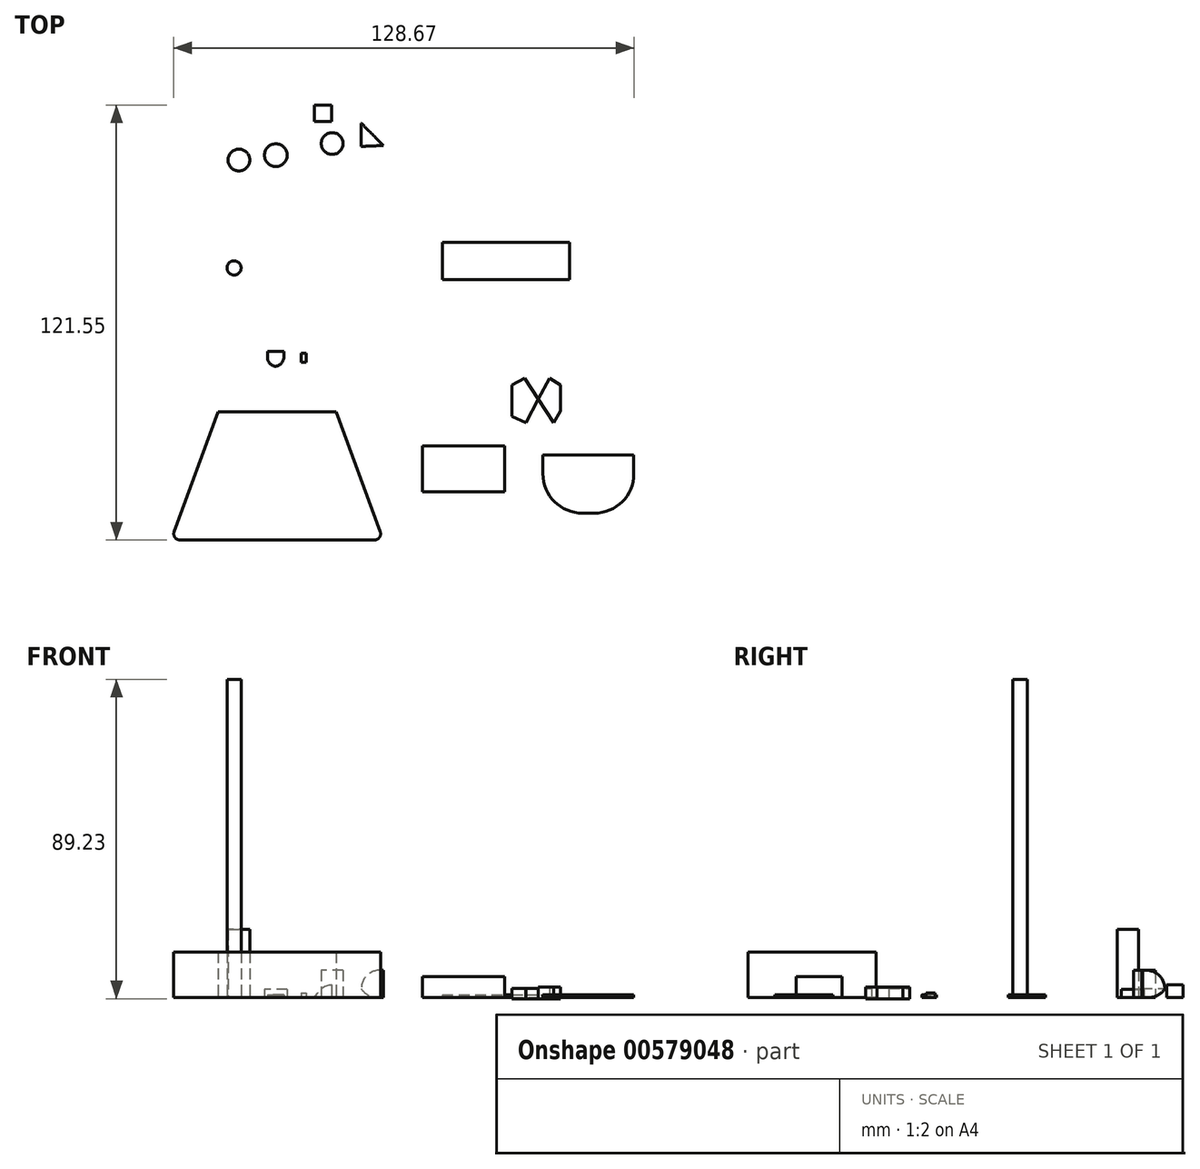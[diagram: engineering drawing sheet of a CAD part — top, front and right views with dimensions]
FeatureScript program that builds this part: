
annotation { "Feature Type Name" : "Feature", "Feature Type Description" : "" }
export const myFeature = defineFeature(function(context is Context, id is Id, definition is map)
    precondition{}
    {
        {
            var Q0;
            Q0=qCreatedBy(makeId("Top.planeOp"),FACE);
            var sketch = newSketch(context, id + "F0", { "sketchPlane" : qUnion([Q0])});
            skLineSegment(sketch, "E0", {"start": v(-46.16, -23.7) * mm, "end": v(-59.3, -59.45) * mm});
            skLineSegment(sketch, "E1", {"start": v(-59.3, -59.45) * mm, "end": v(0, -59.45) * mm});
            skLineSegment(sketch, "E2", {"start": v(0, -59.45) * mm, "end": v(-13.14, -23.7) * mm});
            skLineSegment(sketch, "E3", {"start": v(-13.14, -23.7) * mm, "end": v(-46.16, -23.7) * mm});
            skSolve(sketch);
        }
        {
            var Q0;
            Q0=makeQuery(id+"F0.imprint","IMPRINT",FACE,{"disambiguationData":[TD([[makeQuery(id+"F0.imprint","IMPRINT",EDGE,{"derivedFrom":sQuery(id+"F0.wireOp",EDGE,"E0")}),1.0]])]});
            extrude(context, id + "F1", {"entities" : qUnion([Q0]), "depth" : 12.7 * mm, "offsetDistance" : 25.4 * mm});
        }
        {
            var Q0;
            Q0=makeQuery(id+"F1.opExtrude","SWEPT_EDGE",EDGE,{"disambiguationData":[OSD([sQuery(id+"F0.wireOp",EDGE,"E0"),sQuery(id+"F0.wireOp",EDGE,"E1")])]});
            fillet(context, id + "F2", {"entities" : qUnion([Q0]), "radius" : 1.7 * mm, "tangentPropagation" : true, "allowEdgeOverflow" : false});
        }
        {
            var Q0;
            Q0=makeQuery(id+"F1.opExtrude","SWEPT_EDGE",EDGE,{"disambiguationData":[OSD([sQuery(id+"F0.wireOp",EDGE,"E1"),sQuery(id+"F0.wireOp",EDGE,"E2")])]});
            fillet(context, id + "F3", {"entities" : qUnion([Q0]), "radius" : 1.7 * mm, "tangentPropagation" : true, "allowEdgeOverflow" : false});
        }
        {
            var Q0;
            Q0=qCreatedBy(makeId("Top.planeOp"),FACE);
            var sketch = newSketch(context, id + "F4", { "sketchPlane" : qUnion([Q0])});
            skLineSegment(sketch, "E4.bottom", {"start": v(11.02, -33.17) * mm, "end": v(33.98, -33.17) * mm});
            skLineSegment(sketch, "E4.top", {"start": v(11.02, -46.03) * mm, "end": v(33.98, -46.03) * mm});
            skLineSegment(sketch, "E4.left", {"start": v(11.02, -33.17) * mm, "end": v(11.02, -46.03) * mm});
            skLineSegment(sketch, "E4.right", {"start": v(33.98, -33.17) * mm, "end": v(33.98, -46.03) * mm});
            skSolve(sketch);
        }
        {
            var Q0;
            Q0=makeQuery(id+"F4.imprint","IMPRINT",FACE,{"disambiguationData":[TD([[makeQuery(id+"F4.imprint","IMPRINT",EDGE,{"derivedFrom":sQuery(id+"F4.wireOp",EDGE,"E4.bottom")}),-1.0]])]});
            extrude(context, id + "F5", {"entities" : qUnion([Q0]), "depth" : 0.76 * mm, "offsetDistance" : 25.4 * mm});
        }
        {
            var Q0;
            Q0=qCreatedBy(makeId("Top.planeOp"),FACE);
            var sketch = newSketch(context, id + "F6", { "sketchPlane" : qUnion([Q0])});
            skLineSegment(sketch, "E5.bottom", {"start": v(-27.78, -6.77) * mm, "end": v(-32.37, -6.77) * mm});
            skLineSegment(sketch, "E5.top", {"start": v(-27.78, -10.9) * mm, "end": v(-32.37, -10.9) * mm});
            skLineSegment(sketch, "E5.left", {"start": v(-27.78, -6.77) * mm, "end": v(-27.78, -10.9) * mm});
            skLineSegment(sketch, "E5.right", {"start": v(-32.37, -6.77) * mm, "end": v(-32.37, -10.9) * mm});
            skSolve(sketch);
        }
        {
            var Q0;
            Q0 = qSketchRegion(id + "F6", true);
            extrude(context, id + "F7", {"entities" : qUnion([Q0]), "depth" : 0.76 * mm, "offsetDistance" : 25.4 * mm});
        }
        {
            var Q0;
            Q0=makeQuery(id+"F7.opExtrude","SWEPT_EDGE",EDGE,{"disambiguationData":[OSD([sQuery(id+"F6.wireOp",EDGE,"E5.top"),sQuery(id+"F6.wireOp",EDGE,"E5.left")])]});
            fillet(context, id + "F8", {"entities" : qUnion([Q0]), "radius" : 2.54 * mm, "tangentPropagation" : true, "allowEdgeOverflow" : false});
        }
        {
            var Q0;
            Q0=makeQuery(id+"F7.opExtrude","SWEPT_EDGE",EDGE,{"disambiguationData":[OSD([sQuery(id+"F6.wireOp",EDGE,"E5.top"),sQuery(id+"F6.wireOp",EDGE,"E5.right")])]});
            fillet(context, id + "F9", {"entities" : qUnion([Q0]), "radius" : 2.54 * mm, "tangentPropagation" : true, "allowEdgeOverflow" : false});
        }
        {
            var Q0;
            Q0=qCreatedBy(makeId("Top.planeOp"),FACE);
            var sketch = newSketch(context, id + "F10", { "sketchPlane" : qUnion([Q0])});
            skLineSegment(sketch, "E6.bottom", {"start": v(-22.96, -7.23) * mm, "end": v(-21.58, -7.23) * mm});
            skLineSegment(sketch, "E6.top", {"start": v(-22.96, -9.76) * mm, "end": v(-21.58, -9.76) * mm});
            skLineSegment(sketch, "E6.left", {"start": v(-22.96, -7.23) * mm, "end": v(-22.96, -9.76) * mm});
            skLineSegment(sketch, "E6.right", {"start": v(-21.58, -7.23) * mm, "end": v(-21.58, -9.76) * mm});
            skSolve(sketch);
        }
        {
            var Q0;
            Q0=makeQuery(id+"F10.imprint","IMPRINT",FACE,{"disambiguationData":[TD([[makeQuery(id+"F10.imprint","IMPRINT",EDGE,{"derivedFrom":sQuery(id+"F10.wireOp",EDGE,"E6.bottom")}),-1.0]])]});
            extrude(context, id + "F11", {"entities" : qUnion([Q0]), "depth" : 1.27 * mm, "offsetDistance" : 25.4 * mm});
        }
        {
            var Q0;
            Q0=qCreatedBy(makeId("Top.planeOp"),FACE);
            var sketch = newSketch(context, id + "F12", { "sketchPlane" : qUnion([Q0])});
            skLineSegment(sketch, "E7", {"start": v(43.4, -20.09) * mm, "end": v(49.6, -16.19) * mm});
            skLineSegment(sketch, "E8", {"start": v(49.6, -16.19) * mm, "end": v(49.6, -23.38) * mm});
            skLineSegment(sketch, "E9", {"start": v(49.6, -23.38) * mm, "end": v(43.4, -20.09) * mm});
            skLineSegment(sketch, "E10", {"start": v(43.4, -20.09) * mm, "end": v(36.04, -16.19) * mm});
            skLineSegment(sketch, "E11", {"start": v(36.04, -16.19) * mm, "end": v(36.04, -24.92) * mm});
            skLineSegment(sketch, "E12", {"start": v(36.04, -24.92) * mm, "end": v(43.4, -20.09) * mm});
            skLineSegment(sketch, "E13", {"start": v(43.4, -20.09) * mm, "end": v(46.5, -14.25) * mm});
            skPoint(sketch, "E13.endSnap0", {"position": v(46.5, -18.14) * mm});
            skLineSegment(sketch, "E14", {"start": v(46.5, -14.25) * mm, "end": v(49.6, -16.19) * mm});
            skLineSegment(sketch, "E15", {"start": v(43.4, -20.09) * mm, "end": v(39.56, -14.25) * mm});
            skLineSegment(sketch, "E16", {"start": v(39.56, -14.25) * mm, "end": v(36.04, -16.19) * mm});
            skLineSegment(sketch, "E17", {"start": v(43.4, -20.09) * mm, "end": v(47.7, -26.64) * mm});
            skLineSegment(sketch, "E18", {"start": v(43.4, -20.09) * mm, "end": v(39.91, -26.64) * mm});
            skLineSegment(sketch, "E19", {"start": v(39.91, -26.64) * mm, "end": v(36.04, -24.92) * mm});
            skLineSegment(sketch, "E20", {"start": v(47.7, -26.64) * mm, "end": v(49.6, -23.38) * mm});
            skSolve(sketch);
        }
        {
            var Q0;
            Q0=makeQuery(id+"F12.imprint","IMPRINT",FACE,{"disambiguationData":[TD([[makeQuery(id+"F12.imprint","IMPRINT",EDGE,{"derivedFrom":sQuery(id+"F12.wireOp",EDGE,"E9")}),1.0]])]});
            var Q1;
            Q1=makeQuery(id+"F12.imprint","IMPRINT",FACE,{"disambiguationData":[TD([[makeQuery(id+"F12.imprint","IMPRINT",EDGE,{"derivedFrom":sQuery(id+"F12.wireOp",EDGE,"E10")}),-1.0]])]});
            var Q2;
            Q2=makeQuery(id+"F12.imprint","IMPRINT",FACE,{"disambiguationData":[TD([[makeQuery(id+"F12.imprint","IMPRINT",EDGE,{"derivedFrom":sQuery(id+"F12.wireOp",EDGE,"E12")}),-1.0]])]});
            var Q3;
            Q3=makeQuery(id+"F12.imprint","IMPRINT",FACE,{"disambiguationData":[TD([[makeQuery(id+"F12.imprint","IMPRINT",EDGE,{"derivedFrom":sQuery(id+"F12.wireOp",EDGE,"E7")}),-1.0]])]});
            var Q4;
            Q4=makeQuery(id+"F12.imprint","IMPRINT",FACE,{"disambiguationData":[TD([[makeQuery(id+"F12.imprint","IMPRINT",EDGE,{"derivedFrom":sQuery(id+"F12.wireOp",EDGE,"E10")}),1.0]])]});
            var Q5;
            Q5=makeQuery(id+"F12.imprint","IMPRINT",FACE,{"disambiguationData":[TD([[makeQuery(id+"F12.imprint","IMPRINT",EDGE,{"derivedFrom":sQuery(id+"F12.wireOp",EDGE,"E7")}),1.0]])]});
            extrude(context, id + "F13", {"entities" : qUnion([Q0, Q1, Q2, Q3, Q4, Q5]), "depth" : 1.78 * mm, "offsetDistance" : 25.4 * mm});
        }
        {
            var Q0;
            Q0=qCreatedBy(makeId("Top.planeOp"),FACE);
            var sketch = newSketch(context, id + "F14", { "sketchPlane" : qUnion([Q0])});
            skLineSegment(sketch, "E21.bottom", {"start": v(44.7, -35.7) * mm, "end": v(70.1, -35.7) * mm});
            skLineSegment(sketch, "E21.top", {"start": v(44.7, -52) * mm, "end": v(70.1, -52) * mm});
            skLineSegment(sketch, "E21.left", {"start": v(44.7, -35.7) * mm, "end": v(44.7, -52) * mm});
            skLineSegment(sketch, "E21.right", {"start": v(70.1, -35.7) * mm, "end": v(70.1, -52) * mm});
            skSolve(sketch);
        }
        {
            var Q0;
            Q0=makeQuery(id+"F14.imprint","IMPRINT",FACE,{"disambiguationData":[TD([[makeQuery(id+"F14.imprint","IMPRINT",EDGE,{"derivedFrom":sQuery(id+"F14.wireOp",EDGE,"E21.bottom")}),-1.0]])]});
            extrude(context, id + "F15", {"entities" : qUnion([Q0]), "depth" : 0.76 * mm, "offsetDistance" : 25.4 * mm});
        }
        {
            var Q0;
            Q0=makeQuery(id+"F15.opExtrude","SWEPT_EDGE",EDGE,{"disambiguationData":[OSD([sQuery(id+"F14.wireOp",EDGE,"E21.top"),sQuery(id+"F14.wireOp",EDGE,"E21.left")])]});
            fillet(context, id + "F16", {"entities" : qUnion([Q0]), "radius" : 11.04 * mm, "tangentPropagation" : true, "allowEdgeOverflow" : false});
        }
        {
            var Q0;
            Q0=makeQuery(id+"F15.opExtrude","SWEPT_EDGE",EDGE,{"disambiguationData":[OSD([sQuery(id+"F14.wireOp",EDGE,"E21.top"),sQuery(id+"F14.wireOp",EDGE,"E21.right")])]});
            fillet(context, id + "F17", {"entities" : qUnion([Q0]), "radius" : 11.05 * mm, "tangentPropagation" : true, "allowEdgeOverflow" : false});
        }
        {
            var Q0;
            Q0=qCreatedBy(makeId("Top.planeOp"),FACE);
            var sketch = newSketch(context, id + "F18", { "sketchPlane" : qUnion([Q0])});
            skLineSegment(sketch, "E22.bottom", {"start": v(16.54, 23.67) * mm, "end": v(52.1, 23.67) * mm});
            skLineSegment(sketch, "E22.top", {"start": v(16.54, 13.26) * mm, "end": v(52.1, 13.26) * mm});
            skLineSegment(sketch, "E22.left", {"start": v(16.54, 23.67) * mm, "end": v(16.54, 13.26) * mm});
            skLineSegment(sketch, "E22.right", {"start": v(52.1, 23.67) * mm, "end": v(52.1, 13.26) * mm});
            skSolve(sketch);
        }
        {
            var Q0;
            Q0=makeQuery(id+"F18.imprint","IMPRINT",FACE,{"disambiguationData":[TD([[makeQuery(id+"F18.imprint","IMPRINT",EDGE,{"derivedFrom":sQuery(id+"F18.wireOp",EDGE,"E22.bottom")}),-1.0]])]});
            extrude(context, id + "F19", {"entities" : qUnion([Q0]), "depth" : 0.76 * mm, "offsetDistance" : 25.4 * mm});
        }
        {
            var Q0;
            Q0=makeQuery(id+"F5.opExtrude","CAP_FACE",FACE,{"disambiguationData":[OSD([sQuery(id+"F4.wireOp",EDGE,"E4.bottom"),sQuery(id+"F4.wireOp",EDGE,"E4.top"),sQuery(id+"F4.wireOp",EDGE,"E4.left"),sQuery(id+"F4.wireOp",EDGE,"E4.right")])],"isStart":false});
            extrude(context, id + "F20", {"entities" : qUnion([Q0]), "operationType" : NewBodyOperationType.ADD, "depth" : 5.08 * mm, "offsetDistance" : 25.4 * mm});
        }
        {
            var Q0;
            Q0=qCreatedBy(makeId("Top.planeOp"),FACE);
            var sketch = newSketch(context, id + "F21", { "sketchPlane" : qUnion([Q0])});
            skCircle(sketch, "E23", {"center": v(-40.34, 46.73) * mm, "radius": 3.04 * mm});
            skSolve(sketch);
        }
        {
            var Q0;
            Q0 = qSketchRegion(id + "F21", true);
            extrude(context, id + "F22", {"entities" : qUnion([Q0]), "depth" : 19.05 * mm, "offsetDistance" : 25.4 * mm});
        }
        {
            var Q0;
            Q0=qCreatedBy(makeId("Top.planeOp"),FACE);
            var sketch = newSketch(context, id + "F23", { "sketchPlane" : qUnion([Q0])});
            skCircle(sketch, "E24", {"center": v(-30.02, 48.09) * mm, "radius": 3.18 * mm});
            skSolve(sketch);
        }
        {
            var Q0;
            Q0=makeQuery(id+"F23.imprint","IMPRINT",FACE,{"disambiguationData":[TD([[makeQuery(id+"F23.imprint","IMPRINT",EDGE,{"derivedFrom":sQuery(id+"F23.wireOp",EDGE,"E24")}),1.0]])]});
            extrude(context, id + "F24", {"entities" : qUnion([Q0]), "depth" : 2.3 * mm, "offsetDistance" : 25.4 * mm});
        }
        {
            var Q0;
            Q0=qCreatedBy(makeId("Top.planeOp"),FACE);
            var sketch = newSketch(context, id + "F25", { "sketchPlane" : qUnion([Q0])});
            skCircle(sketch, "E25", {"center": v(-14.26, 51.35) * mm, "radius": 3.04 * mm});
            skSolve(sketch);
        }
        {
            var Q0;
            Q0=makeQuery(id+"F25.imprint","IMPRINT",FACE,{"disambiguationData":[TD([[makeQuery(id+"F25.imprint","IMPRINT",EDGE,{"derivedFrom":sQuery(id+"F25.wireOp",EDGE,"E25")}),1.0]])]});
            extrude(context, id + "F26", {"entities" : qUnion([Q0]), "depth" : 7.62 * mm, "offsetDistance" : 25.4 * mm});
        }
        {
            var Q0;
            Q0=qCreatedBy(makeId("Top.planeOp"),FACE);
            var sketch = newSketch(context, id + "F27", { "sketchPlane" : qUnion([Q0])});
            skLineSegment(sketch, "E26", {"start": v(-6.11, 50.53) * mm, "end": v(-6.11, 57.05) * mm});
            skLineSegment(sketch, "E27", {"start": v(-6.11, 57.05) * mm, "end": v(0, 50.8) * mm});
            skLineSegment(sketch, "E28", {"start": v(0, 50.8) * mm, "end": v(-6.11, 50.53) * mm});
            skSolve(sketch);
        }
        {
            var Q0;
            Q0=makeQuery(id+"F27.imprint","IMPRINT",FACE,{"disambiguationData":[TD([[makeQuery(id+"F27.imprint","IMPRINT",EDGE,{"derivedFrom":sQuery(id+"F27.wireOp",EDGE,"E26")}),-1.0]])]});
            extrude(context, id + "F28", {"entities" : qUnion([Q0]), "depth" : 7.62 * mm, "offsetDistance" : 25.4 * mm});
        }
        {
            var Q0;
            Q0=makeQuery(id+"F28.opExtrude","CAP_EDGE",EDGE,{"disambiguationData":[OSD([sQuery(id+"F27.wireOp",EDGE,"E26")])],"isStart":false});
            fillet(context, id + "F29", {"entities" : qUnion([Q0]), "radius" : 5.08 * mm, "tangentPropagation" : true, "allowEdgeOverflow" : false});
        }
        {
            var Q0;
            Q0=makeQuery(id+"F28.opExtrude","CAP_EDGE",EDGE,{"disambiguationData":[OSD([sQuery(id+"F27.wireOp",EDGE,"E26")])],"isStart":true});
            fillet(context, id + "F30", {"entities" : qUnion([Q0]), "radius" : 5.08 * mm, "tangentPropagation" : true, "allowEdgeOverflow" : false});
        }
        {
            var Q0;
            Q0=qCreatedBy(makeId("Top.planeOp"),FACE);
            var sketch = newSketch(context, id + "F31", { "sketchPlane" : qUnion([Q0])});
            skLineSegment(sketch, "E29.bottom", {"start": v(-19.78, 62.1) * mm, "end": v(-14.45, 62.1) * mm});
            skLineSegment(sketch, "E29.top", {"start": v(-19.78, 57.52) * mm, "end": v(-14.45, 57.52) * mm});
            skLineSegment(sketch, "E29.left", {"start": v(-19.78, 62.1) * mm, "end": v(-19.78, 57.52) * mm});
            skLineSegment(sketch, "E29.right", {"start": v(-14.45, 62.1) * mm, "end": v(-14.45, 57.52) * mm});
            skSolve(sketch);
        }
        {
            var Q0;
            Q0=makeQuery(id+"F31.imprint","IMPRINT",FACE,{"disambiguationData":[TD([[makeQuery(id+"F31.imprint","IMPRINT",EDGE,{"derivedFrom":sQuery(id+"F31.wireOp",EDGE,"E29.bottom")}),-1.0]])]});
            extrude(context, id + "F32", {"entities" : qUnion([Q0]), "depth" : 3.56 * mm, "offsetDistance" : 25.4 * mm});
        }
        {
            var Q0;
            Q0=makeQuery(id+"F32.opExtrude","CAP_EDGE",EDGE,{"disambiguationData":[OSD([sQuery(id+"F31.wireOp",EDGE,"E29.left")])],"isStart":false});
            fillet(context, id + "F33", {"entities" : qUnion([Q0]), "radius" : 6.13 * mm, "tangentPropagation" : true, "allowEdgeOverflow" : false});
        }
        {
            var Q0;
            Q0=qCreatedBy(makeId("Top.planeOp"),FACE);
            var sketch = newSketch(context, id + "F34", { "sketchPlane" : qUnion([Q0])});
            skCircle(sketch, "E30", {"center": v(-41.7, 16.57) * mm, "radius": 1.98 * mm});
            skSolve(sketch);
        }
        {
            var Q0;
            Q0=makeQuery(id+"F34.imprint","IMPRINT",FACE,{"disambiguationData":[TD([[makeQuery(id+"F34.imprint","IMPRINT",EDGE,{"derivedFrom":sQuery(id+"F34.wireOp",EDGE,"E30")}),1.0]])]});
            extrude(context, id + "F35", {"entities" : qUnion([Q0]), "depth" : 88.9 * mm, "offsetDistance" : 25.4 * mm});
        }
        {
            var Q0;
            Q0=qCreatedBy(makeId("Top.planeOp"),FACE);
            var sketch = newSketch(context, id + "F36", { "sketchPlane" : qUnion([Q0])});
            skLineSegment(sketch, "E31", {"start": v(24.87, 29.22) * mm, "end": v(24.87, 54.62) * mm});
            skLineSegment(sketch, "E32", {"start": v(24.87, 54.62) * mm, "end": v(55.35, 54.62) * mm});
            skLineSegment(sketch, "E33", {"start": v(55.35, 54.62) * mm, "end": v(55.35, 29.22) * mm});
            skSolve(sketch);
        }
        {
            var Q0;
            Q0=sQuery(id+"F36.wireOp",EDGE,"E31");
            var Q1;
            Q1=sQuery(id+"F36.wireOp",EDGE,"E32");
            var Q2;
            Q2=sQuery(id+"F36.wireOp",EDGE,"E33");
            extrude(context, id + "F37", {"bodyType" : ToolBodyType.SURFACE, "surfaceEntities" : qUnion([Q0, Q1, Q2]), "depth" : 2.03 * mm, "offsetDistance" : 25.4 * mm});
        }
        {
            var Q0;
            Q0=makeQuery(id+"F13.opExtrude","CAP_FACE",FACE,{"disambiguationData":[OSD([sQuery(id+"F12.wireOp",EDGE,"E11"),sQuery(id+"F12.wireOp",EDGE,"E15"),sQuery(id+"F12.wireOp",EDGE,"E16"),sQuery(id+"F12.wireOp",EDGE,"E18"),sQuery(id+"F12.wireOp",EDGE,"E19")])],"isStart":true});
            var Q1;
            Q1=makeQuery(id+"F13.opExtrude","CAP_FACE",FACE,{"disambiguationData":[OSD([sQuery(id+"F12.wireOp",EDGE,"E8"),sQuery(id+"F12.wireOp",EDGE,"E13"),sQuery(id+"F12.wireOp",EDGE,"E14"),sQuery(id+"F12.wireOp",EDGE,"E17"),sQuery(id+"F12.wireOp",EDGE,"E20")])],"isStart":true});
            extrude(context, id + "F38", {"entities" : qUnion([Q0, Q1]), "operationType" : NewBodyOperationType.ADD, "depth" : 0.33 * mm, "offsetDistance" : 25.4 * mm, "hasSecondDirection" : true, "secondDirectionOppositeDirection" : true, "secondDirectionDepth" : 2.54 * mm});
        }
        {
            var Q0;
            Q0=makeQuery(id+"F38.opExtrude","CAP_FACE",FACE,{"disambiguationData":[OSD([sQuery(id+"F12.wireOp",EDGE,"E8"),sQuery(id+"F12.wireOp",EDGE,"E13"),sQuery(id+"F12.wireOp",EDGE,"E14"),sQuery(id+"F12.wireOp",EDGE,"E17"),sQuery(id+"F12.wireOp",EDGE,"E20")])],"isStart":true});
            extrude(context, id + "F39", {"entities" : qUnion([Q0]), "operationType" : NewBodyOperationType.ADD, "depth" : 0.33 * mm, "offsetDistance" : 25.4 * mm, "hasSecondDirection" : true, "secondDirectionOppositeDirection" : true, "secondDirectionDepth" : 2.54 * mm});
        }
    });
